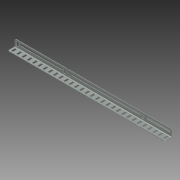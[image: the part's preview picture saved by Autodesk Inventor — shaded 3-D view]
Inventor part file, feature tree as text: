
AUTODESK INVENTOR PART (.ipt)
format: ipt  version: 2013 (Build 170138000, 138)  size: 581,632 bytes
history: native  units: mm (DEFAULTED — no unit token found)
features: other x64, extrude x61, sketch x6, sheet_metal_op x3, pattern_linear x1
ambient origin geometry x8: Origin, YZ Plane, XZ Plane, XY Plane, X Axis, Y Axis, Z Axis, Center Point
bodies: Solid1 (feature_tree)
feature tree (135):
  sheet_metal_op  "Face1"
  sheet_metal_op  "Flange1"
  other  "Corner Chamfer1"
  extrude  "Extrusion1"  Depth=9.779mm
  pattern_linear  "Rectangular Pattern1"  Spacing1=1.905mm  [1 undecoded]
  sketch  "Sketch1"  dims[d1=4.064mm d2=9.779mm]
  other  "Plate1"
  sketch  "Sketch2"  dims[d3=4.572mm]
  other  "Plate2"
  sheet_metal_op  "Bend1"
  sketch  "Sketch3"  dims[d12=16.51mm]
  sketch  "Sketch4"  dims[d14=1.905mm]
  sketch  "Sketch5"  dims[d15=1.905mm]
  other  "Srf1"
  sketch  "Sketch6"  dims[d16=1.905mm d17=1.905mm d18=300.0mm d20=12.7mm d21=10.0mm d23=25.4mm d25=4.064mm d26=1.905mm d27=1.905mm d28=1.905mm d29=1.905mm d30=1.27mm d31=1.27mm d32=0.635mm d33=2.54mm d34=1.27mm d35=16.51mm d36=90.0deg d37=0.8636mm d38=1.905mm d39=6.35mm d40=45.0deg d41=3.302mm d42=4.064mm d43=4.572mm d45=1.905mm d46=1.905mm d47=0.0mm d48=4.064mm d49=4.572mm d50=3.429mm d51=9.779mm d52=3.048mm d53=4.572mm d54=177.8mm d55=3.048mm d56=4.572mm d58=1.905mm d59=1.905mm d60=0.0mm d61=4.064mm d62=4.064mm d63=4.572mm d64=3.048mm d65=4.064mm d67=3.048mm d68=4.572mm d69=1.27mm d70=0.0mm d71=0.508mm d72=0.508mm d73=13.208mm d74=3.81mm d75=3.048mm d76=0.0mm d77=0.508mm d78=0.508mm d79=3.81mm d80=13.208mm d81=3.302mm d82=25.4mm d83=0.0mm d84=25.4mm d85=0.0mm d86=300.0mm d88=12.7mm d89=0.0mm d90=0.0mm d91=0.0mm d92=0.0mm d93=0.0mm d94=0.0mm d95=0.0mm d96=0.0mm d97=0.0mm d98=0.0mm d99=0.0mm d100=0.0mm d101=0.0mm d102=0.0mm d103=0.0mm d104=0.0mm d105=0.0mm d106=0.0mm d107=0.0mm d108=0.0mm d109=0.0mm d110=0.0mm d111=0.0mm d112=0.0mm d113=0.0mm d114=0.0mm d115=0.0mm d116=0.0mm d117=0.0mm d118=0.0mm d119=0.0mm d120=0.0mm d121=0.0mm d122=0.0mm d123=0.0mm d124=0.0mm d125=0.0mm d126=0.0mm d127=0.0mm d128=0.0mm d129=0.0mm d130=0.0mm d131=0.0mm d132=0.0mm d133=0.0mm d134=0.0mm d135=0.0mm d136=0.0mm d137=0.0mm d138=0.0mm d139=0.0mm d140=0.0mm d141=0.0mm d142=0.0mm d143=0.0mm d144=0.0mm d145=0.0mm d146=0.0mm d147=0.0mm d148=0.0mm d149=0.0mm d150=0.0mm d151=0.0mm d152=0.0mm d153=0.0mm d154=0.0mm d155=0.0mm d156=0.0mm d157=0.0mm d158=0.0mm d159=0.0mm d160=0.0mm d161=0.0mm d162=0.0mm d163=0.0mm d164=0.0mm d165=0.0mm d166=0.0mm d167=0.0mm d168=0.0mm d169=0.0mm d170=0.0mm d171=0.0mm d172=0.0mm d173=0.0mm d174=0.0mm d175=0.0mm d176=0.0mm d177=0.0mm d178=0.0mm d179=0.0mm d180=0.0mm d181=0.0mm d182=0.0mm d183=0.0mm d184=0.0mm d185=0.0mm d186=0.0mm d187=0.0mm d188=0.0mm d189=0.0mm d190=0.0mm d191=0.0mm d192=0.0mm d193=0.0mm d194=0.0mm d195=0.0mm d196=0.0mm d197=0.0mm d198=0.0mm d199=0.0mm d200=0.0mm d201=0.0mm d202=0.0mm]
  other  "Srf2"
  other  "Srf4"
  other  "Srf6"
  other  "Srf8"
  other  "Srf10"
  other  "Srf12"
  other  "Srf14"
  other  "Srf16"
  other  "Srf18"
  other  "Srf20"
  other  "Srf22"
  other  "Srf24"
  other  "Srf26"
  other  "Srf28"
  other  "Srf30"
  other  "Srf32"
  other  "Srf34"
  other  "Srf36"
  other  "Srf38"
  other  "Srf40"
  other  "Srf42"
  other  "Srf44"
  other  "Srf46"
  other  "Srf48"
  other  "Srf50"
  other  "Srf52"
  other  "Srf54"
  other  "Srf56"
  other  "Srf58"
  other  "Srf60"
  other  "Srf3"
  other  "Srf5"
  other  "Srf7"
  other  "Srf9"
  other  "Srf11"
  other  "Srf13"
  other  "Srf15"
  other  "Srf17"
  other  "Srf19"
  other  "Srf21"
  other  "Srf23"
  other  "Srf25"
  other  "Srf27"
  other  "Srf29"
  other  "Srf31"
  other  "Srf33"
  other  "Srf35"
  other  "Srf37"
  other  "Srf39"
  other  "Srf41"
  other  "Srf43"
  other  "Srf45"
  other  "Srf47"
  other  "Srf49"
  other  "Srf51"
  other  "Srf53"
  other  "Srf55"
  other  "Srf57"
  other  "Srf59"
  other  "Cut1"
  extrude  "ExtrusionSrf1"  Depth=300.0mm
  extrude  "ExtrusionSrf2"  Depth=4.064mm
  extrude  "ExtrusionSrf3"  Depth=1.905mm
  extrude  "ExtrusionSrf4"  Depth=1.905mm
  extrude  "ExtrusionSrf5"  Depth=1.905mm
  extrude  "ExtrusionSrf6"  Depth=1.905mm
  extrude  "ExtrusionSrf7"  Depth=1.27mm
  extrude  "ExtrusionSrf8"  Depth=1.27mm
  extrude  "ExtrusionSrf9"  Depth=0.635mm
  extrude  "ExtrusionSrf10"  Depth=2.54mm
  extrude  "ExtrusionSrf11"  Depth=1.27mm
  extrude  "ExtrusionSrf12"  Depth=16.51mm TaperAngle=90.0deg
  extrude  "ExtrusionSrf13"  Depth=1.905mm TaperAngle=45.0deg
  extrude  "ExtrusionSrf14"  Depth=3.302mm
  extrude  "ExtrusionSrf15"  Depth=4.064mm
  extrude  "ExtrusionSrf16"  Depth=4.572mm
  extrude  "ExtrusionSrf17"  Depth=1.905mm
  extrude  "ExtrusionSrf18"  Depth=1.905mm
  extrude  "ExtrusionSrf19"  TaperAngle=0.0deg  [1 undecoded]
  extrude  "ExtrusionSrf20"  Depth=4.064mm
  extrude  "ExtrusionSrf21"  Depth=4.572mm
  extrude  "ExtrusionSrf22"  Depth=3.429mm
  extrude  "ExtrusionSrf23"  Depth=9.779mm
  extrude  "ExtrusionSrf24"  Depth=3.048mm
  extrude  "ExtrusionSrf25"  Depth=4.572mm
  extrude  "ExtrusionSrf26"  Depth=177.8mm
  extrude  "ExtrusionSrf27"  Depth=3.048mm
  extrude  "ExtrusionSrf28"  Depth=4.572mm
  extrude  "ExtrusionSrf29"  Depth=1.905mm
  extrude  "ExtrusionSrf30"  Depth=1.905mm
  extrude  "ExtrusionSrf31"  TaperAngle=0.0deg  [1 undecoded]
  extrude  "ExtrusionSrf32"  Depth=4.064mm
  extrude  "ExtrusionSrf33"  Depth=4.064mm
  extrude  "ExtrusionSrf34"  Depth=4.572mm
  extrude  "ExtrusionSrf35"  Depth=3.048mm
  extrude  "ExtrusionSrf36"  Depth=4.064mm
  extrude  "ExtrusionSrf37"  Depth=3.048mm
  extrude  "ExtrusionSrf38"  Depth=4.572mm
  extrude  "ExtrusionSrf39"  Depth=1.27mm
  extrude  "ExtrusionSrf40"  TaperAngle=0.0deg  [1 undecoded]
  extrude  "ExtrusionSrf41"  Depth=0.508mm
  extrude  "ExtrusionSrf42"  Depth=0.508mm
  extrude  "ExtrusionSrf43"  Depth=13.208mm
  extrude  "ExtrusionSrf44"  Depth=3.81mm
  extrude  "ExtrusionSrf45"  Depth=3.048mm TaperAngle=0.0deg
  extrude  "ExtrusionSrf46"  Depth=0.508mm
  extrude  "ExtrusionSrf47"  Depth=0.508mm
  extrude  "ExtrusionSrf48"  Depth=3.81mm
  extrude  "ExtrusionSrf49"  Depth=13.208mm
  extrude  "ExtrusionSrf50"  Depth=3.302mm
  extrude  "ExtrusionSrf51"  Depth=25.4mm TaperAngle=0.0deg
  extrude  "ExtrusionSrf52"  Depth=25.4mm TaperAngle=0.0deg
  extrude  "ExtrusionSrf53"  Depth=300.0mm
  extrude  "ExtrusionSrf54"  TaperAngle=0.0deg  [1 undecoded]
  extrude  "ExtrusionSrf55"  TaperAngle=0.0deg  [1 undecoded]
  extrude  "ExtrusionSrf56"  TaperAngle=0.0deg  [1 undecoded]
  extrude  "ExtrusionSrf57"  TaperAngle=0.0deg  [1 undecoded]
  extrude  "ExtrusionSrf58"  TaperAngle=0.0deg  [1 undecoded]
  extrude  "ExtrusionSrf59"  TaperAngle=0.0deg  [1 undecoded]
  extrude  "ExtrusionSrf60"  TaperAngle=0.0deg  [1 undecoded]
note: 11 required parameter values undecoded (feature->parameter linkage not recoverable at this tier; creation-order binding heuristic only, values carry confidence <= 0.55)
